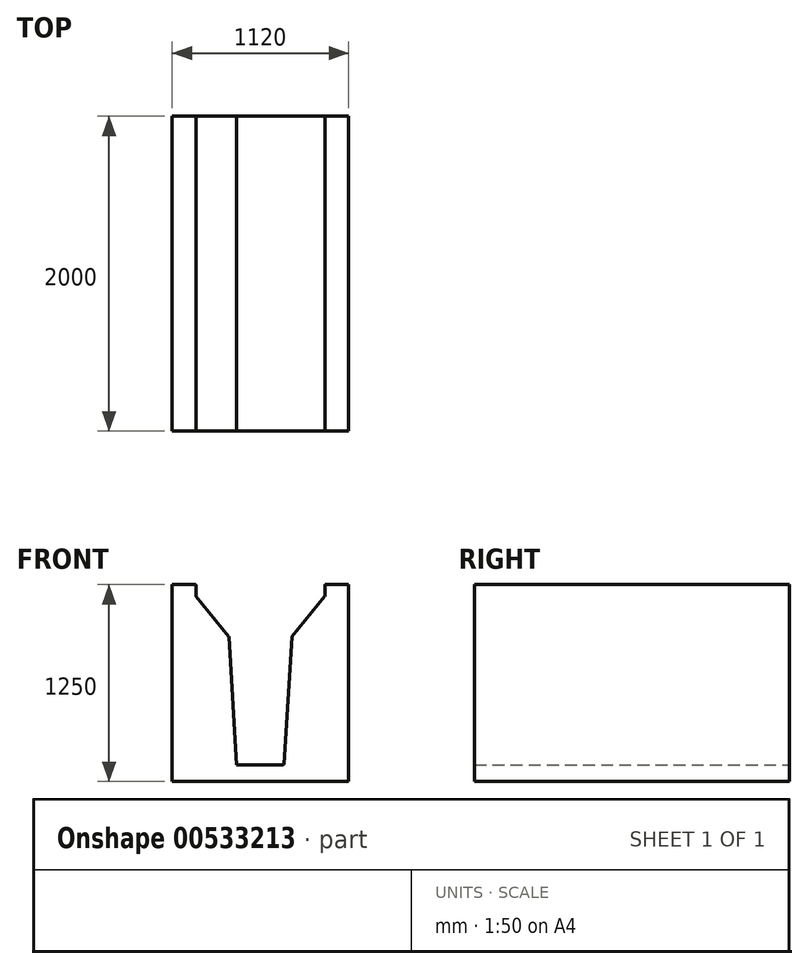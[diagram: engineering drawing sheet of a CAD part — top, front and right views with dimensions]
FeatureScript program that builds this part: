
annotation { "Feature Type Name" : "Feature", "Feature Type Description" : "" }
export const myFeature = defineFeature(function(context is Context, id is Id, definition is map)
    precondition{}
    {
        {
            var Q0;
            Q0=qCreatedBy(makeId("Front.planeOp"),FACE);
            var sketch = newSketch(context, id + "F0", { "sketchPlane" : qUnion([Q0])});
            skLineSegment(sketch, "E0", {"start": v(0, 0) * mm, "end": v(150, 0) * mm});
            skLineSegment(sketch, "E1", {"start": v(150, 0) * mm, "end": v(200, 814) * mm});
            skLineSegment(sketch, "E2", {"start": v(200, 814) * mm, "end": v(410, 1069) * mm});
            skLineSegment(sketch, "E3", {"start": v(410, 1069) * mm, "end": v(410, 1144) * mm});
            skLineSegment(sketch, "E4", {"start": v(410, 1144) * mm, "end": v(560, 1144) * mm});
            skLineSegment(sketch, "E5", {"start": v(560, 1144) * mm, "end": v(560, -106) * mm});
            skLineSegment(sketch, "E6", {"start": v(560, -106) * mm, "end": v(0, -106) * mm});
            skLineSegment(sketch, "E7.MirrorCS", {"start": v(-560, 1144) * mm, "end": v(-560, -106) * mm});
            skLineSegment(sketch, "E8.MirrorCS", {"start": v(-150, 0) * mm, "end": v(-200, 814) * mm});
            skLineSegment(sketch, "E9.MirrorCS", {"start": v(-410, 1069) * mm, "end": v(-410, 1144) * mm});
            skLineSegment(sketch, "E10.MirrorCS", {"start": v(-410, 1144) * mm, "end": v(-560, 1144) * mm});
            skLineSegment(sketch, "E11.MirrorCS", {"start": v(-200, 814) * mm, "end": v(-410, 1069) * mm});
            skLineSegment(sketch, "E12.MirrorCS", {"start": v(-560, -106) * mm, "end": v(0, -106) * mm});
            skLineSegment(sketch, "E13.MirrorCS", {"start": v(0, 0) * mm, "end": v(-150, 0) * mm});
            skSolve(sketch);
        }
        {
            var Q0;
            Q0 = qSketchRegion(id + "F0", true);
            extrude(context, id + "F1", {"entities" : qUnion([Q0]), "depth" : 2000 * mm, "offsetDistance" : 25 * mm});
        }
        {
            var Q0;
            Q0=makeQuery(id+"F1.opExtrude","SWEPT_EDGE",EDGE,{"disambiguationData":[OSD([sQuery(id+"F0.wireOp",EDGE,"E8.MirrorCS"),sQuery(id+"F0.wireOp",EDGE,"E11.MirrorCS")])]});
            fillet(context, id + "F2", {"entities" : qUnion([Q0]), "radius" : 5 * mm, "tangentPropagation" : true, "allowEdgeOverflow" : false});
        }
        {
            var Q0;
            Q0=makeQuery(id+"F1.opExtrude","SWEPT_EDGE",EDGE,{"disambiguationData":[OSD([sQuery(id+"F0.wireOp",EDGE,"E9.MirrorCS"),sQuery(id+"F0.wireOp",EDGE,"E11.MirrorCS")])]});
            fillet(context, id + "F3", {"entities" : qUnion([Q0]), "radius" : 5 * mm, "tangentPropagation" : true, "allowEdgeOverflow" : false});
        }
        {
            var Q0;
            Q0=makeQuery(id+"F1.opExtrude","SWEPT_EDGE",EDGE,{"disambiguationData":[OSD([sQuery(id+"F0.wireOp",EDGE,"E9.MirrorCS"),sQuery(id+"F0.wireOp",EDGE,"E10.MirrorCS")])]});
            fillet(context, id + "F4", {"entities" : qUnion([Q0]), "radius" : 5 * mm, "tangentPropagation" : true, "allowEdgeOverflow" : false});
        }
        {
            var Q0;
            Q0=makeQuery(id+"F1.opExtrude","SWEPT_EDGE",EDGE,{"disambiguationData":[OSD([sQuery(id+"F0.wireOp",EDGE,"E3"),sQuery(id+"F0.wireOp",EDGE,"E4")])]});
            var Q1;
            Q1=makeQuery(id+"F1.opExtrude","SWEPT_EDGE",EDGE,{"disambiguationData":[OSD([sQuery(id+"F0.wireOp",EDGE,"E1"),sQuery(id+"F0.wireOp",EDGE,"E2")])]});
            var Q2;
            Q2=makeQuery(id+"F1.opExtrude","SWEPT_EDGE",EDGE,{"disambiguationData":[OSD([sQuery(id+"F0.wireOp",EDGE,"E0"),sQuery(id+"F0.wireOp",EDGE,"E1")])]});
            var Q3;
            Q3=makeQuery(id+"F1.opExtrude","SWEPT_EDGE",EDGE,{"disambiguationData":[OSD([sQuery(id+"F0.wireOp",EDGE,"E2"),sQuery(id+"F0.wireOp",EDGE,"E3")])]});
            fillet(context, id + "F5", {"entities" : qUnion([Q0, Q1, Q2, Q3]), "radius" : 5 * mm, "tangentPropagation" : true, "allowEdgeOverflow" : false});
        }
    });
